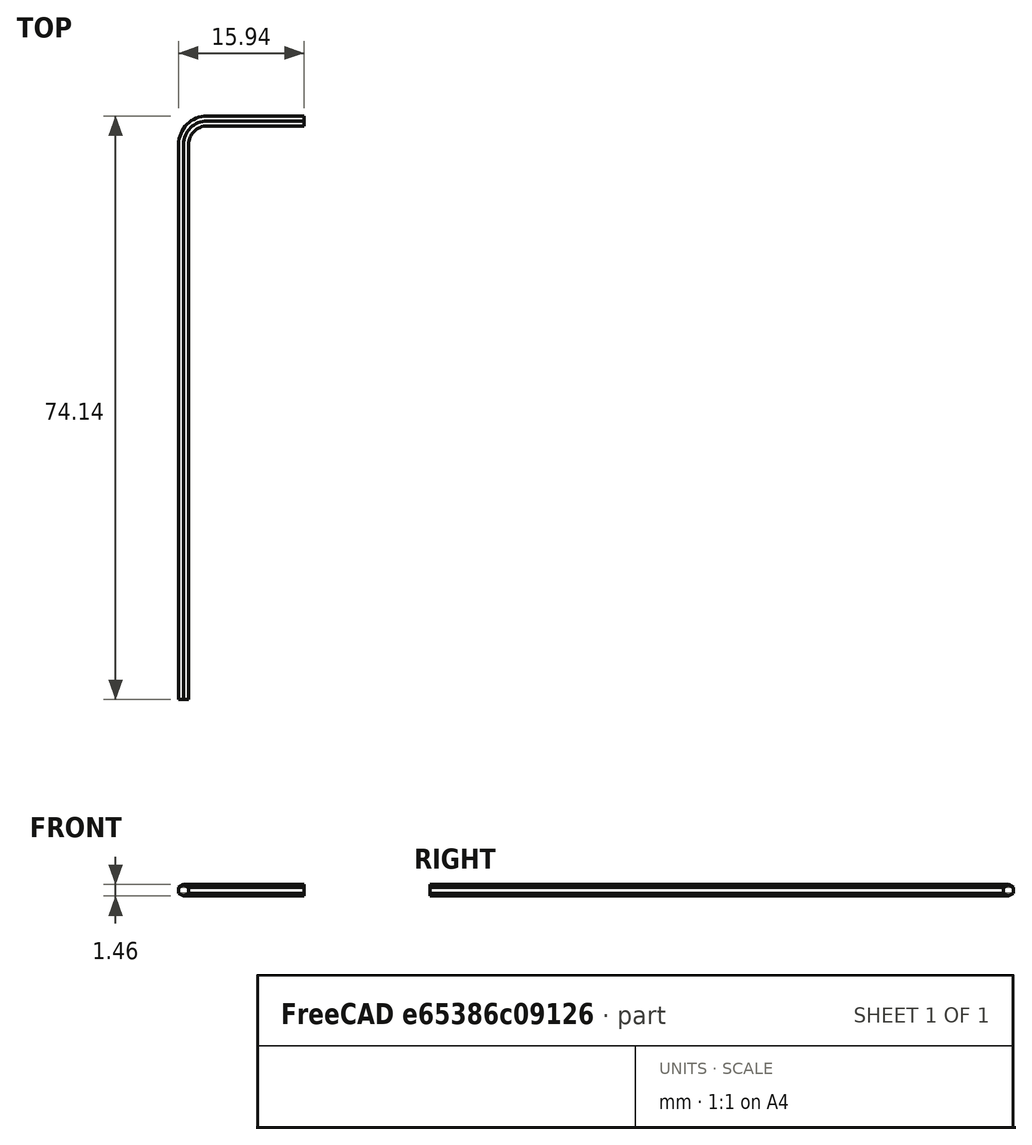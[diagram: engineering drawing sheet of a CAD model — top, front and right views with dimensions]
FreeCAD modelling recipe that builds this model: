
FCSTD DOCUMENT  (FreeCAD 0.19R22261 (Git))
Label: allen_key
License: All rights reserved
LicenseURL: http://en.wikipedia.org/wiki/All_rights_reserved
objects: App::DocumentObjectGroup×2, PartDesign::CoordinateSystem×2, Sketcher::SketchObject×2, App::FeaturePython×1, PartDesign::AdditivePipe×1, PartDesign::Body×1, App::Part×1
note: 7 computed .brp shape members not serialized (recipe doc carries the construction recipe); baked Part::Feature solids carry a one-line shape summary decoded from their .brp

FEATURE [App::DocumentObjectGroup] Parts
FEATURE [PartDesign::CoordinateSystem] LCS_Origin
  AttacherType = Attacher::AttachEngine3D
  MapMode = 2
  Support = -> [X_Axis]
FEATURE [App::DocumentObjectGroup] Constraints
FEATURE [App::FeaturePython] Variables  # WARN: FeaturePython — macro-defined, semantics opaque (R4)
FEATURE [PartDesign::CoordinateSystem] LCS_0
  AttacherType = Attacher::AttachEngine3D
  MapMode = 2
  Support = -> [X_Axis001]
FEATURE [Sketcher::SketchObject] Sketch  label="hex"
  MapMode = 5
  Placement = pos=(0,0,0) rot=(0.57735,0.57735,0.57735;2.0944rad)
  Support = -> [YZ_Plane001]
  sketch-geometry (7):
    g0: LineSegment StartX=0 StartY=0.733235 StartZ=0 EndX=-0.635 EndY=0.366617 EndZ=0
    g1: LineSegment StartX=-0.635 StartY=0.366617 StartZ=0 EndX=-0.635 EndY=-0.366617 EndZ=0
    g2: LineSegment StartX=-0.635 StartY=-0.366617 StartZ=0 EndX=0 EndY=-0.733235 EndZ=0
    g3: LineSegment StartX=0 StartY=-0.733235 StartZ=0 EndX=0.635 EndY=-0.366617 EndZ=0
    g4: LineSegment StartX=0.635 StartY=-0.366617 StartZ=0 EndX=0.635 EndY=0.366617 EndZ=0
    g5: LineSegment StartX=0.635 StartY=0.366617 StartZ=0 EndX=0 EndY=0.733235 EndZ=0
    g6: Circle [constr] CenterX=0 CenterY=0 CenterZ=0 NormalX=0 NormalY=0 NormalZ=1 AngleXU=0 Radius=0.733235
  constraints (16):
    c: Coincident(g0,g1)
    c: Coincident(g1,g2)
    c: Coincident(g2,g3)
    c: Coincident(g3,g4)
    c: Coincident(g4,g5)
    c: Coincident(g5,g0)
    c: Equal(g0, g1-g5) x5
    c: PointOnObject(g0,g6)
    c: PointOnObject(g1,g6)
    c: PointOnObject(g2,g6)
    c: PointOnObject(g3,g6)
    c: PointOnObject(g4,g6)
    c: PointOnObject(g5,g6)
    c: Coincident(g6,g-1)
    c: Vertical(g0,g-1)
    c: Distance(g3,g1) = 1.27
FEATURE [Sketcher::SketchObject] Sketch001  label="path"
  MapMode = 5
  Support = -> [XY_Plane001]
  sketch-geometry (3):
    g0: LineSegment StartX=0 StartY=0 StartZ=0 EndX=-12.3 EndY=0 EndZ=0
    g1: LineSegment StartX=-15.3 StartY=-3 StartZ=0 EndX=-15.3 EndY=-73.5 EndZ=0
    g2: ArcOfCircle CenterX=-12.3 CenterY=-3 CenterZ=0 NormalX=0 NormalY=0 NormalZ=1 AngleXU=0 Radius=3 StartAngle=1.5708 EndAngle=3.14159
  constraints (8):
    c: Coincident(g-1,g0)
    c: Vertical(g1)
    c: Tangent(g0,g2) = -1.5708
    c: Tangent(g1,g2) = -1.5708
    c: DistanceX(g1,g0) = 15.3
    c: DistanceY(g1,g0) = 73.5
    c: Horizontal(g0)
    c: Radius(g2) = 3
FEATURE [PartDesign::AdditivePipe] AdditivePipe
  AuxilleryCurvelinear = true
  AuxillerySpineTangent = false
  Binormal = (0,0,0)
  Mode = 0
  Placement = pos=(0,0,0) rot=(0.57735,0.57735,0.57735;2.0944rad)
  Profile = -> Sketch
  Spine = -> Sketch001
  SpineTangent = false
  Transformation = 0
  Transition = 0
FEATURE [PartDesign::Body] Body
  Group = -> [LCS_0,Sketch,Sketch001,AdditivePipe]
  Origin = -> Origin001
  Tip = -> AdditivePipe
FEATURE [App::Part] Model
  Configuration = 0
  Group = -> [LCS_Origin,Constraints,Variables,Body]
  Origin = -> Origin
  Type = Assembly4 Model
